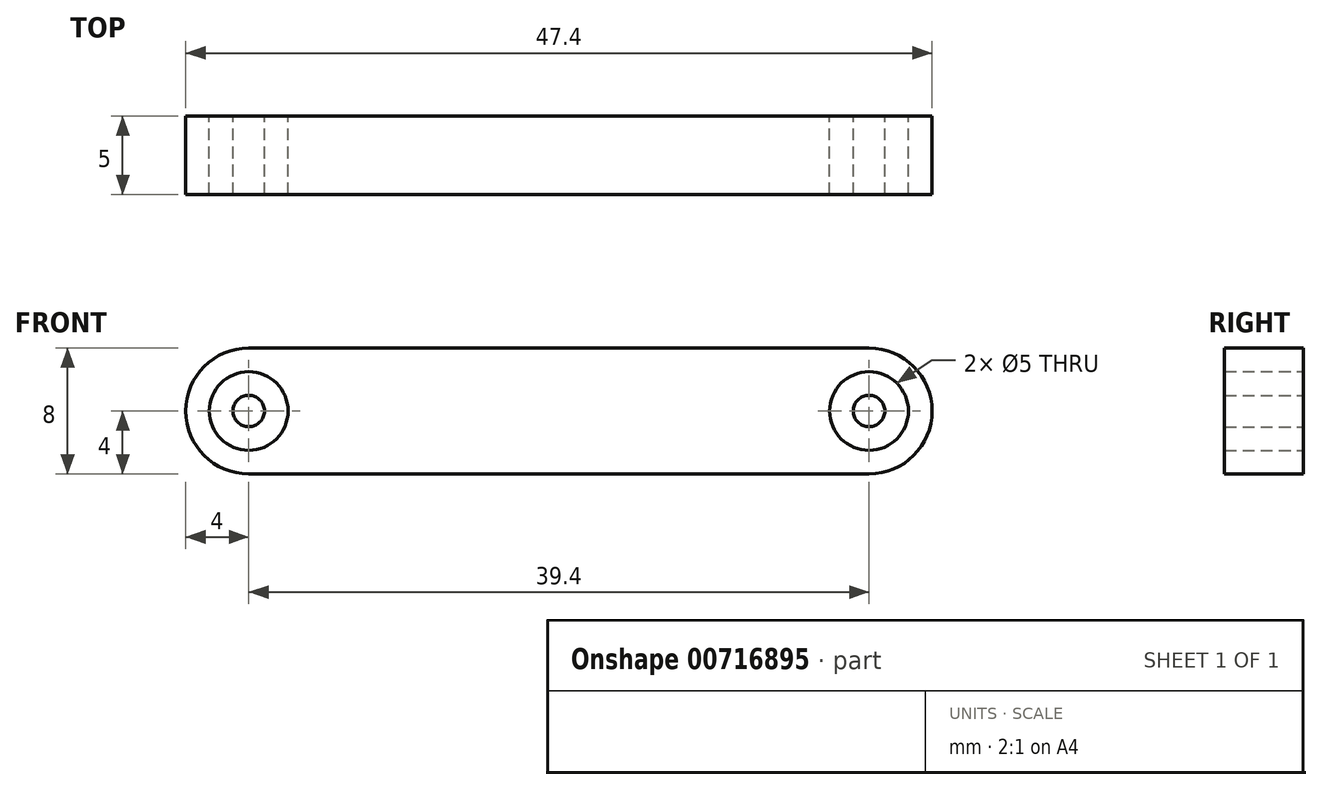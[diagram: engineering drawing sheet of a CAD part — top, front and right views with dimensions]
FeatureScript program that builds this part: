
annotation { "Feature Type Name" : "Feature", "Feature Type Description" : "" }
export const myFeature = defineFeature(function(context is Context, id is Id, definition is map)
    precondition{}
    {
        {
            var Q0;
            Q0=qCreatedBy(makeId("Front.planeOp"),FACE);
            var sketch = newSketch(context, id + "F0", { "sketchPlane" : qUnion([Q0])});
            skArc(sketch, "E0", {"start": v(0, -4) * mm, "mid": v(4, 0) * mm, "end": v(0, 4) * mm});
            skArc(sketch, "E1", {"start": v(-39.4, 4) * mm, "mid": v(-43.4, 0) * mm, "end": v(-39.4, -4) * mm});
            skLineSegment(sketch, "E2", {"start": v(0, 4) * mm, "end": v(-39.4, 4) * mm});
            skLineSegment(sketch, "E3", {"start": v(0, -4) * mm, "end": v(-39.4, -4) * mm});
            skCircle(sketch, "E4", {"center": v(-39.4, 0) * mm, "radius": 2.5 * mm});
            skCircle(sketch, "E5", {"center": v(-39.4, 0) * mm, "radius": 1 * mm});
            skCircle(sketch, "E6", {"center": v(0, 0) * mm, "radius": 1 * mm});
            skCircle(sketch, "E7", {"center": v(0, 0) * mm, "radius": 2.5 * mm});
            skSolve(sketch);
        }
        {
            var Q0;
            Q0 = qSketchRegion(id + "F0", true);
            var Q1;
            Q1=makeQuery(id+"F0.imprint","IMPRINT",FACE,{"disambiguationData":[TD([[makeQuery(id+"F0.imprint","IMPRINT",EDGE,{"derivedFrom":sQuery(id+"F0.wireOp",EDGE,"E5")}),1.0]])]});
            var Q2;
            Q2=makeQuery(id+"F0.imprint","IMPRINT",FACE,{"disambiguationData":[TD([[makeQuery(id+"F0.imprint","IMPRINT",EDGE,{"derivedFrom":sQuery(id+"F0.wireOp",EDGE,"E6")}),1.0]])]});
            extrude(context, id + "F1", {"entities" : qUnion([Q0, Q1, Q2]), "depth" : 5 * mm, "offsetDistance" : 25.4 * mm});
        }
    });
